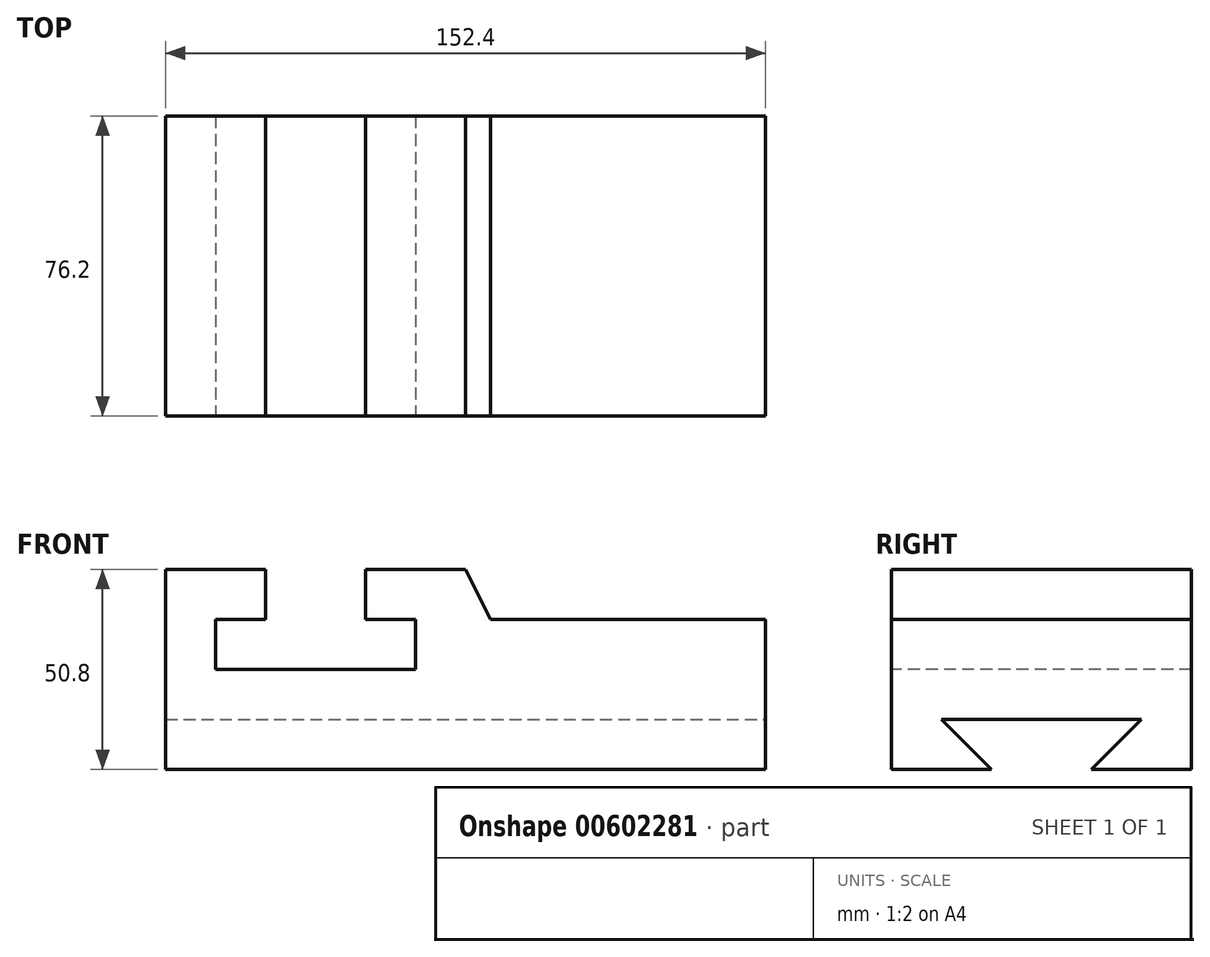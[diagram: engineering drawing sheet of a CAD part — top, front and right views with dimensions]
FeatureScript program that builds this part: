
annotation { "Feature Type Name" : "Feature", "Feature Type Description" : "" }
export const myFeature = defineFeature(function(context is Context, id is Id, definition is map)
    precondition{}
    {
        {
            var Q0;
            Q0=qCreatedBy(makeId("Front.planeOp"),FACE);
            var sketch = newSketch(context, id + "F0", { "sketchPlane" : qUnion([Q0])});
            skLineSegment(sketch, "E0", {"start": v(0, 0) * mm, "end": v(152.4, 0) * mm});
            skLineSegment(sketch, "E1", {"start": v(152.4, 0) * mm, "end": v(152.4, 50.8) * mm});
            skLineSegment(sketch, "E2", {"start": v(152.4, 50.8) * mm, "end": v(0, 50.8) * mm});
            skLineSegment(sketch, "E3", {"start": v(0, 50.8) * mm, "end": v(0, 0) * mm});
            skSolve(sketch);
        }
        {
            var Q0;
            Q0 = qSketchRegion(id + "F0", true);
            extrude(context, id + "F1", {"entities" : qUnion([Q0]), "depth" : 76.2 * mm, "offsetDistance" : 25.4 * mm});
        }
        {
            var Q0;
            Q0=makeQuery(id+"F1.opExtrude","CAP_FACE",FACE,{"disambiguationData":[OSD([sQuery(id+"F0.wireOp",EDGE,"E0"),sQuery(id+"F0.wireOp",EDGE,"E1"),sQuery(id+"F0.wireOp",EDGE,"E2"),sQuery(id+"F0.wireOp",EDGE,"E3")])],"isStart":false});
            var sketch = newSketch(context, id + "F2", { "sketchPlane" : qUnion([Q0])});
            skLineSegment(sketch, "E4", {"start": v(0, 50.8) * mm, "end": v(25.4, 50.8) * mm});
            skLineSegment(sketch, "E5", {"start": v(25.4, 50.8) * mm, "end": v(25.4, 38.1) * mm});
            skLineSegment(sketch, "E6", {"start": v(25.4, 38.1) * mm, "end": v(12.7, 38.1) * mm});
            skLineSegment(sketch, "E7", {"start": v(12.7, 38.1) * mm, "end": v(12.7, 25.4) * mm});
            skLineSegment(sketch, "E8", {"start": v(12.7, 25.4) * mm, "end": v(63.5, 25.4) * mm});
            skLineSegment(sketch, "E9", {"start": v(63.5, 25.4) * mm, "end": v(63.5, 38.1) * mm});
            skPoint(sketch, "E9.endSnap0", {"position": v(19.05, 38.1) * mm});
            skLineSegment(sketch, "E10", {"start": v(63.5, 38.1) * mm, "end": v(50.8, 38.1) * mm});
            skLineSegment(sketch, "E11", {"start": v(50.8, 38.1) * mm, "end": v(50.8, 50.8) * mm});
            skSolve(sketch);
        }
        {
            var Q0;
            {var subQ0=sQuery(id+"F2.wireOp",EDGE,"E5");Q0=makeQuery(id+"F2.imprint","IMPRINT",FACE,{"disambiguationData":[TD([[makeQuery(id+"F2.imprint","IMPRINT",EDGE,{"derivedFrom":subQ0}),1.0]])]});}
            extrude(context, id + "F3", {"entities" : qUnion([Q0]), "operationType" : NewBodyOperationType.REMOVE, "oppositeDirection" : true, "depth" : 254 * mm, "offsetDistance" : 25.4 * mm});
        }
        {
            var Q0;
            Q0=makeQuery(id+"F1.opExtrude","SWEPT_FACE",FACE,{"disambiguationData":[OSD([sQuery(id+"F0.wireOp",EDGE,"E1")])]});
            var sketch = newSketch(context, id + "F4", { "sketchPlane" : qUnion([Q0])});
            skLineSegment(sketch, "E12", {"start": v(-38.1, 12.7) * mm, "end": v(-63.5, 12.7) * mm});
            skLineSegment(sketch, "E13", {"start": v(-38.1, 12.7) * mm, "end": v(-12.7, 12.7) * mm});
            skPoint(sketch, "E13.endSnap0", {"position": v(-12.7, 0) * mm});
            skLineSegment(sketch, "E14", {"start": v(-63.5, 12.7) * mm, "end": v(-50.8, 0) * mm});
            skLineSegment(sketch, "E15", {"start": v(-12.7, 12.7) * mm, "end": v(-25.4, 0) * mm});
            skSolve(sketch);
        }
        {
            var Q0;
            Q0=makeQuery(id+"F4.imprint","IMPRINT",FACE,{"disambiguationData":[TD([[makeQuery(id+"F4.imprint","IMPRINT",EDGE,{"derivedFrom":sQuery(id+"F4.wireOp",EDGE,"E12")}),1.0]])]});
            var sketch = newSketch(context, id + "F5", { "sketchPlane" : qUnion([Q0])});
            skSolve(sketch);
        }
        {
            var Q0;
            Q0 = qSketchRegion(id + "F5", true);
            var Q1;
            Q1=makeQuery(id+"F4.imprint","IMPRINT",FACE,{"disambiguationData":[TD([[makeQuery(id+"F4.imprint","IMPRINT",EDGE,{"derivedFrom":sQuery(id+"F4.wireOp",EDGE,"E12")}),1.0]])]});
            extrude(context, id + "F6", {"entities" : qUnion([Q0, Q1]), "operationType" : NewBodyOperationType.REMOVE, "oppositeDirection" : true, "depth" : 508 * mm, "offsetDistance" : 25.4 * mm});
        }
        {
            var Q0;
            Q0=makeQuery(id+"F1.opExtrude","CAP_FACE",FACE,{"disambiguationData":[OSD([sQuery(id+"F0.wireOp",EDGE,"E0"),sQuery(id+"F0.wireOp",EDGE,"E1"),sQuery(id+"F0.wireOp",EDGE,"E2"),sQuery(id+"F0.wireOp",EDGE,"E3")])],"isStart":false});
            var sketch = newSketch(context, id + "F7", { "sketchPlane" : qUnion([Q0])});
            skLineSegment(sketch, "E16", {"start": v(50.8, 50.8) * mm, "end": v(76.2, 50.8) * mm});
            skLineSegment(sketch, "E17", {"start": v(152.4, 38.1) * mm, "end": v(82.55, 38.1) * mm});
            skLineSegment(sketch, "E18", {"start": v(76.2, 50.8) * mm, "end": v(82.55, 38.1) * mm});
            skSolve(sketch);
        }
        {
            var Q0;
            {var subQ0=sQuery(id+"F7.wireOp",EDGE,"E17");Q0=makeQuery(id+"F7.imprint","IMPRINT",FACE,{"disambiguationData":[TD([[makeQuery(id+"F7.imprint","IMPRINT",EDGE,{"derivedFrom":subQ0}),-1.0]])]});}
            extrude(context, id + "F8", {"entities" : qUnion([Q0]), "operationType" : NewBodyOperationType.REMOVE, "oppositeDirection" : true, "depth" : 254 * mm, "offsetDistance" : 25.4 * mm});
        }
    });
